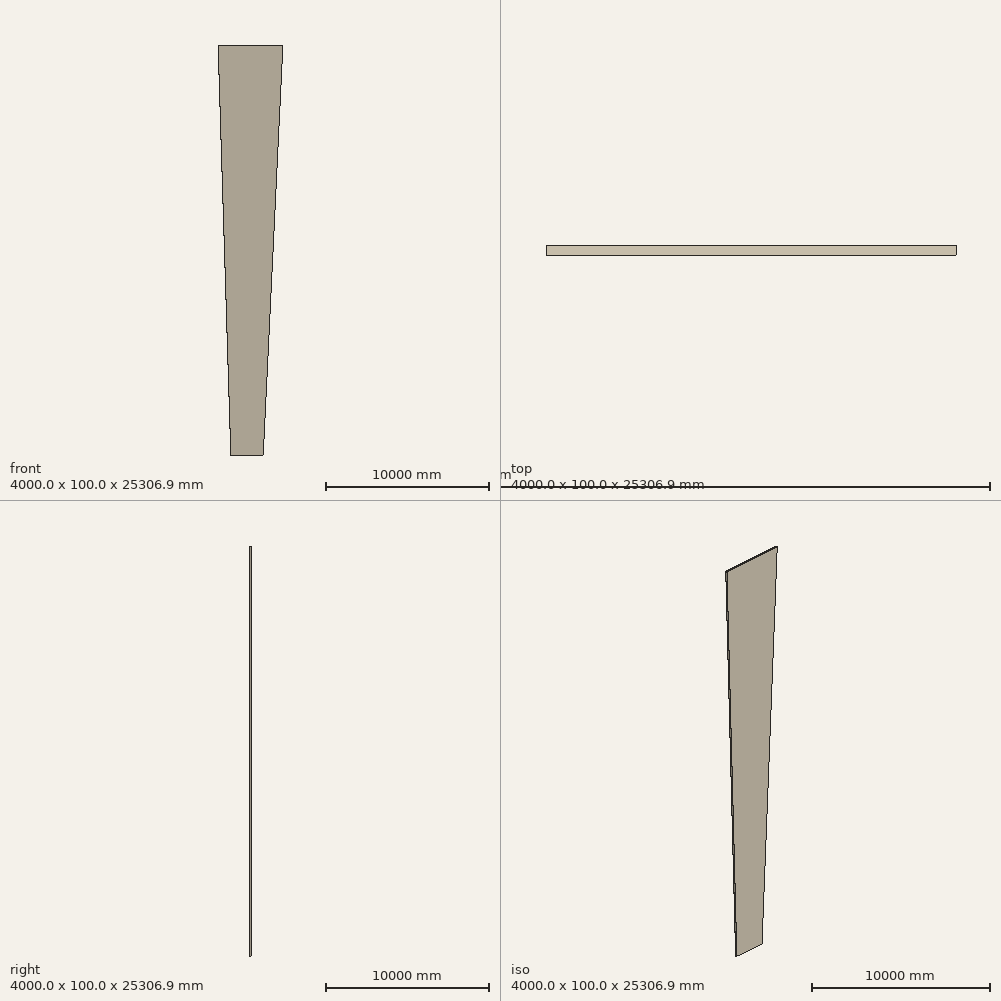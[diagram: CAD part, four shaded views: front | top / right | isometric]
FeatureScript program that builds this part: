
annotation { "Feature Type Name" : "Feature", "Feature Type Description" : "" }
export const myFeature = defineFeature(function(context is Context, id is Id, definition is map)
    precondition{}
    {
        {
            var Q0;
            Q0=qCreatedBy(makeId("Front.planeOp"),FACE);
            var sketch = newSketch(context, id + "F0", { "sketchPlane" : qUnion([Q0])});
            skLineSegment(sketch, "E0", {"start": v(-1785.82, 14621.95) * mm, "end": v(2214.18, 14621.95) * mm});
            skLineSegment(sketch, "E1", {"start": v(1000, -10684.96) * mm, "end": v(-1000, -10668.03) * mm});
            skLineSegment(sketch, "E2", {"start": v(2214.18, 14621.95) * mm, "end": v(1000, -10684.96) * mm});
            skLineSegment(sketch, "E3", {"start": v(-1785.82, 14621.95) * mm, "end": v(-1000, -10668.03) * mm});
            skSolve(sketch);
        }
        {
            var Q0;
            Q0=makeQuery(id+"F0.imprint","IMPRINT",FACE,{"disambiguationData":[TD([[makeQuery(id+"F0.imprint","IMPRINT",EDGE,{"derivedFrom":sQuery(id+"F0.wireOp",EDGE,"E0")}),-1.0]])]});
            extrude(context, id + "F1", {"entities" : qUnion([Q0]), "depth" : 100 * mm, "offsetDistance" : 25 * mm});
        }
    });
